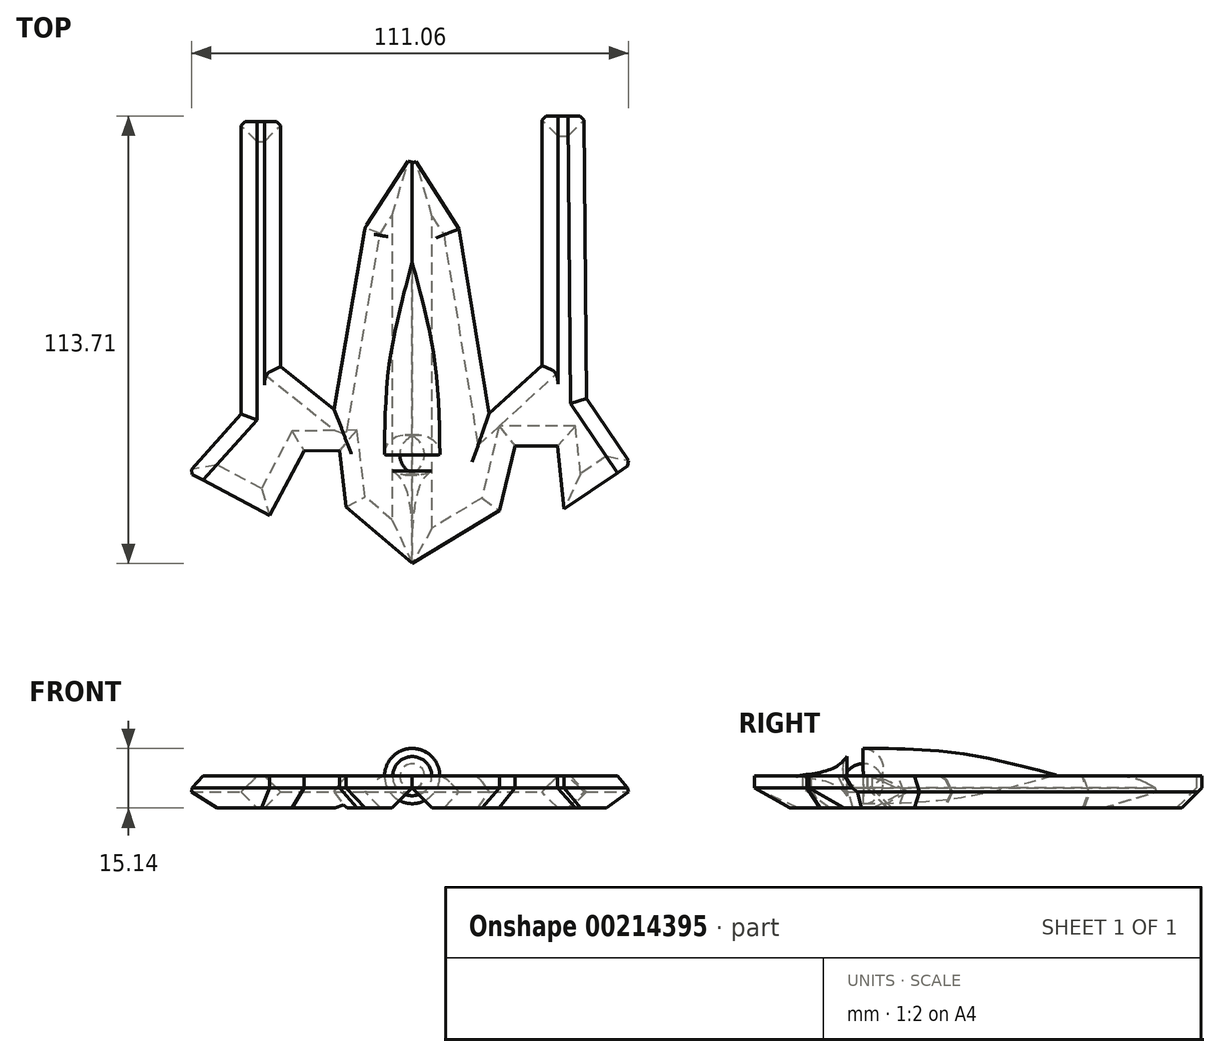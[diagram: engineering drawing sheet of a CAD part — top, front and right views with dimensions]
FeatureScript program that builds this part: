
annotation { "Feature Type Name" : "Feature", "Feature Type Description" : "" }
export const myFeature = defineFeature(function(context is Context, id is Id, definition is map)
    precondition{}
    {
        {
            var Q0;
            Q0=qCreatedBy(makeId("Top.planeOp"),FACE);
            var sketch = newSketch(context, id + "F0", { "sketchPlane" : qUnion([Q0])});
            skLineSegment(sketch, "E0", {"start": v(0, 44.54) * mm, "end": v(12.9, 24.37) * mm});
            skLineSegment(sketch, "E1", {"start": v(12.9, 24.37) * mm, "end": v(20.23, -20.93) * mm});
            skLineSegment(sketch, "E2", {"start": v(20.23, -20.93) * mm, "end": v(20.23, -20.93) * mm});
            skLineSegment(sketch, "E3", {"start": v(20.23, -20.93) * mm, "end": v(31.93, -10.24) * mm});
            skLineSegment(sketch, "E4", {"start": v(31.93, -10.24) * mm, "end": v(31.93, -10.24) * mm});
            skLineSegment(sketch, "E5", {"start": v(31.93, -10.24) * mm, "end": v(31.93, 52.74) * mm});
            skLineSegment(sketch, "E6", {"start": v(31.93, 52.74) * mm, "end": v(44.63, 52.74) * mm});
            skLineSegment(sketch, "E7", {"start": v(44.63, 52.74) * mm, "end": v(45.25, -18.77) * mm});
            skLineSegment(sketch, "E8", {"start": v(45.25, -18.77) * mm, "end": v(56.36, -35.07) * mm});
            skLineSegment(sketch, "E9", {"start": v(56.36, -35.07) * mm, "end": v(38.61, -47.17) * mm});
            skLineSegment(sketch, "E10", {"start": v(38.61, -47.17) * mm, "end": v(36.92, -31.15) * mm});
            skLineSegment(sketch, "E11", {"start": v(36.92, -31.15) * mm, "end": v(26.08, -31.15) * mm});
            skPoint(sketch, "E11.endSnap0", {"position": v(26.08, -15.58) * mm});
            skLineSegment(sketch, "E12", {"start": v(26.08, -31.15) * mm, "end": v(22.14, -47.58) * mm});
            skLineSegment(sketch, "E13", {"start": v(22.14, -47.58) * mm, "end": v(0, -60.97) * mm});
            skLineSegment(sketch, "E14", {"start": v(0, -60.97) * mm, "end": v(0, 44.54) * mm});
            skSolve(sketch);
        }
        {
            var Q0;
            Q0=qCreatedBy(makeId("Top.planeOp"),FACE);
            var sketch = newSketch(context, id + "F1", { "sketchPlane" : qUnion([Q0])});
            skLineSegment(sketch, "E15", {"start": v(0, 44.65) * mm, "end": v(-12.93, 24.7) * mm});
            skLineSegment(sketch, "E16", {"start": v(-12.93, 24.7) * mm, "end": v(-20.5, -19.97) * mm});
            skLineSegment(sketch, "E17", {"start": v(-20.5, -19.97) * mm, "end": v(-32.45, -10.44) * mm});
            skLineSegment(sketch, "E18", {"start": v(-32.45, -10.44) * mm, "end": v(-32.45, 51.3) * mm});
            skLineSegment(sketch, "E19", {"start": v(-32.45, 51.3) * mm, "end": v(-32.45, 51.3) * mm});
            skLineSegment(sketch, "E20", {"start": v(-32.45, 51.3) * mm, "end": v(-44.5, 51.3) * mm});
            skLineSegment(sketch, "E21", {"start": v(-44.5, 51.3) * mm, "end": v(-44.5, 51.3) * mm});
            skLineSegment(sketch, "E22", {"start": v(-44.5, 51.3) * mm, "end": v(-44.5, -22.6) * mm});
            skLineSegment(sketch, "E23", {"start": v(-44.5, -22.6) * mm, "end": v(-57.7, -37.35) * mm});
            skLineSegment(sketch, "E24", {"start": v(-57.7, -37.35) * mm, "end": v(-36.2, -48.81) * mm});
            skLineSegment(sketch, "E25", {"start": v(-36.2, -48.81) * mm, "end": v(-27.46, -32.4) * mm});
            skLineSegment(sketch, "E26", {"start": v(-27.46, -32.4) * mm, "end": v(-18.51, -32.26) * mm});
            skLineSegment(sketch, "E27", {"start": v(-18.51, -32.26) * mm, "end": v(-16.81, -46.65) * mm});
            skLineSegment(sketch, "E28", {"start": v(-16.81, -46.65) * mm, "end": v(0, -60.87) * mm});
            skLineSegment(sketch, "E29", {"start": v(0, -60.87) * mm, "end": v(0, 44.65) * mm});
            skSolve(sketch);
        }
        {
            var Q0;
            Q0 = qSketchRegion(id + "F1", true);
            var Q1;
            Q1=makeQuery(id+"F0.imprint","IMPRINT",FACE,{"disambiguationData":[TD([[makeQuery(id+"F0.imprint","IMPRINT",EDGE,{"derivedFrom":sQuery(id+"F0.wireOp",EDGE,"E0")}),-1.0]])]});
            extrude(context, id + "F9", {"entities" : qUnion([Q0, Q1]), "depth" : 8.14 * mm});
        }
        {
            var Q0;
            Q0=makeQuery(id+"F9.opExtrude","CAP_EDGE",EDGE,{"disambiguationData":[OSD([sQuery(id+"F0.wireOp",EDGE,"E0")])],"isStart":false});
            var Q1;
            Q1=makeQuery(id+"F9.opExtrude","CAP_EDGE",EDGE,{"disambiguationData":[OSD([sQuery(id+"F0.wireOp",EDGE,"E1")])],"isStart":false});
            var Q2;
            Q2=makeQuery(id+"F9.opExtrude","CAP_EDGE",EDGE,{"disambiguationData":[OSD([sQuery(id+"F1.wireOp",EDGE,"E15")])],"isStart":false});
            var Q3;
            Q3=makeQuery(id+"F9.opExtrude","CAP_EDGE",EDGE,{"disambiguationData":[OSD([sQuery(id+"F1.wireOp",EDGE,"E16")])],"isStart":false});
            chamfer(context, id + "F2", {"entities" : qUnion([Q0, Q1, Q2, Q3]), "width" : 5.08 * mm, "tangentPropagation" : true});
        }
        {
            var Q0;
            Q0=makeQuery(id+"F9.opExtrude","CAP_EDGE",EDGE,{"disambiguationData":[OSD([sQuery(id+"F0.wireOp",EDGE,"E5")])],"isStart":false});
            chamfer(context, id + "F3", {"entities" : qUnion([Q0]), "width" : 5.08 * mm, "tangentPropagation" : true});
        }
        {
            var Q0;
            Q0=makeQuery(id+"F9.opExtrude","CAP_EDGE",EDGE,{"disambiguationData":[OSD([sQuery(id+"F0.wireOp",EDGE,"E7")])],"isStart":false});
            chamfer(context, id + "F10", {"entities" : qUnion([Q0]), "width" : 5.08 * mm, "tangentPropagation" : true});
        }
        {
            var Q0;
            Q0=makeQuery(id+"F9.opExtrude","CAP_EDGE",EDGE,{"disambiguationData":[OSD([sQuery(id+"F0.wireOp",EDGE,"E8")])],"isStart":false});
            chamfer(context, id + "F11", {"entities" : qUnion([Q0]), "width" : 5.08 * mm, "tangentPropagation" : true});
        }
        {
            var Q0;
            Q0=makeQuery(id+"F9.opExtrude","CAP_EDGE",EDGE,{"disambiguationData":[OSD([sQuery(id+"F1.wireOp",EDGE,"E23")])],"isStart":false});
            var Q1;
            Q1=makeQuery(id+"F9.opExtrude","CAP_EDGE",EDGE,{"disambiguationData":[OSD([sQuery(id+"F1.wireOp",EDGE,"E22")])],"isStart":false});
            chamfer(context, id + "F4", {"entities" : qUnion([Q0, Q1]), "width" : 5.08 * mm, "tangentPropagation" : true});
        }
        {
            var Q0;
            Q0=makeQuery(id+"F9.opExtrude","CAP_EDGE",EDGE,{"disambiguationData":[OSD([sQuery(id+"F1.wireOp",EDGE,"E18")])],"isStart":false});
            var Q1;
            Q1=makeQuery(id+"F9.opExtrude","CAP_EDGE",EDGE,{"disambiguationData":[OSD([sQuery(id+"F1.wireOp",EDGE,"E17")])],"isStart":false});
            chamfer(context, id + "F5", {"entities" : qUnion([Q0, Q1]), "width" : 5.08 * mm, "tangentPropagation" : true});
        }
        {
            var Q0;
            Q0=makeQuery(id+"F9.opExtrude","CAP_EDGE",EDGE,{"disambiguationData":[OSD([sQuery(id+"F0.wireOp",EDGE,"E3")])],"isStart":false});
            chamfer(context, id + "F6", {"entities" : qUnion([Q0]), "width" : 5.08 * mm, "tangentPropagation" : true});
        }
        {
            var Q0;
            Q0=makeQuery(id+"F9.opExtrude","CAP_FACE",FACE,{"disambiguationData":[OSD([sQuery(id+"F1.wireOp",EDGE,"E15"),sQuery(id+"F1.wireOp",EDGE,"E16"),sQuery(id+"F1.wireOp",EDGE,"E17"),sQuery(id+"F1.wireOp",EDGE,"E18"),sQuery(id+"F1.wireOp",EDGE,"E20"),sQuery(id+"F1.wireOp",EDGE,"E22"),sQuery(id+"F1.wireOp",EDGE,"E23"),sQuery(id+"F1.wireOp",EDGE,"E24"),sQuery(id+"F1.wireOp",EDGE,"E25"),sQuery(id+"F1.wireOp",EDGE,"E26"),sQuery(id+"F1.wireOp",EDGE,"E27"),sQuery(id+"F1.wireOp",EDGE,"E28"),sQuery(id+"F1.wireOp",EDGE,"E29")])],"isStart":true});
            chamfer(context, id + "F12", {"entities" : qUnion([Q0]), "width" : 5.08 * mm, "tangentPropagation" : true});
        }
        {
            var Q0;
            Q0=makeQuery(id+"F9.opExtrude","CAP_FACE",FACE,{"disambiguationData":[OSD([sQuery(id+"F0.wireOp",EDGE,"E0"),sQuery(id+"F0.wireOp",EDGE,"E1"),sQuery(id+"F0.wireOp",EDGE,"E3"),sQuery(id+"F0.wireOp",EDGE,"E5"),sQuery(id+"F0.wireOp",EDGE,"E6"),sQuery(id+"F0.wireOp",EDGE,"E7"),sQuery(id+"F0.wireOp",EDGE,"E8"),sQuery(id+"F0.wireOp",EDGE,"E9"),sQuery(id+"F0.wireOp",EDGE,"E10"),sQuery(id+"F0.wireOp",EDGE,"E11"),sQuery(id+"F0.wireOp",EDGE,"E12"),sQuery(id+"F0.wireOp",EDGE,"E13"),sQuery(id+"F0.wireOp",EDGE,"E14")])],"isStart":true});
            chamfer(context, id + "F13", {"entities" : qUnion([Q0]), "width" : 5.08 * mm, "tangentPropagation" : true});
        }
        {
            var Q0;
            Q0=qCreatedBy(makeId("Right.planeOp"),FACE);
            var sketch = newSketch(context, id + "F14", { "sketchPlane" : qUnion([Q0])});
            skFitSpline(sketch, "E30", {"points": [v(15.67, 8.43) * mm, v(-10.4, 14.09) * mm, v(-36.13, 15.13) * mm], "startDerivative": vector(-51.62, 13.53) * mm, "endDerivative": vector(-51.98, -0.16) * mm});
            skFitSpline(sketch, "E31", {"points": [v(-36.13, 15.13) * mm, v(-40.25, 10.5) * mm, v(-52.55, 8) * mm], "startDerivative": vector(-7.72, -12.68) * mm, "endDerivative": vector(-24.16, -2.19) * mm});
            skLineSegment(sketch, "E32", {"start": v(-52.55, 8) * mm, "end": v(15.67, 8.43) * mm});
            skSolve(sketch);
        }
        {
            var Q0;
            Q0=makeQuery(id+"F14.imprint","IMPRINT",FACE,{"disambiguationData":[TD([[makeQuery(id+"F14.imprint","IMPRINT",EDGE,{"derivedFrom":sQuery(id+"F14.wireOp",EDGE,"E30")}),1.0]])]});
            var Q1;
            Q1=sQuery(id+"F14.wireOp",EDGE,"E32");
            revolve(context, id + "F15", {"entities" : qUnion([Q0]), "axis" : qUnion([Q1]), "revolveType" : RevolveType.FULL});
        }
        {
            var Q0;
            {var subQ0=sQuery(id+"F1.wireOp",EDGE,"E16");Q0=makeQuery(id+"F2.opChamfer","BLEND_EDGE",EDGE,{"blendedFrom":[makeQuery(id+"F9.opExtrude","CAP_EDGE",EDGE,{"disambiguationData":[OSD([subQ0])],"isStart":false}),makeQuery(id+"F9.opExtrude","CAP_FACE",FACE,{"disambiguationData":[OSD([sQuery(id+"F1.wireOp",EDGE,"E15"),subQ0,sQuery(id+"F1.wireOp",EDGE,"E17"),sQuery(id+"F1.wireOp",EDGE,"E18"),sQuery(id+"F1.wireOp",EDGE,"E20"),sQuery(id+"F1.wireOp",EDGE,"E22"),sQuery(id+"F1.wireOp",EDGE,"E23"),sQuery(id+"F1.wireOp",EDGE,"E24"),sQuery(id+"F1.wireOp",EDGE,"E25"),sQuery(id+"F1.wireOp",EDGE,"E26"),sQuery(id+"F1.wireOp",EDGE,"E27"),sQuery(id+"F1.wireOp",EDGE,"E28"),sQuery(id+"F1.wireOp",EDGE,"E29")])],"isStart":false})],"blendedInto":[makeQuery(id+"F9.opExtrude","CAP_FACE",FACE,{"disambiguationData":[OSD([sQuery(id+"F1.wireOp",EDGE,"E15"),subQ0,sQuery(id+"F1.wireOp",EDGE,"E17"),sQuery(id+"F1.wireOp",EDGE,"E18"),sQuery(id+"F1.wireOp",EDGE,"E20"),sQuery(id+"F1.wireOp",EDGE,"E22"),sQuery(id+"F1.wireOp",EDGE,"E23"),sQuery(id+"F1.wireOp",EDGE,"E24"),sQuery(id+"F1.wireOp",EDGE,"E25"),sQuery(id+"F1.wireOp",EDGE,"E26"),sQuery(id+"F1.wireOp",EDGE,"E27"),sQuery(id+"F1.wireOp",EDGE,"E28"),sQuery(id+"F1.wireOp",EDGE,"E29")])],"isStart":false})]});}
            fillet(context, id + "F16", {"entities" : qUnion([Q0]), "radius" : 5.08 * mm, "tangentPropagation" : true, "allowEdgeOverflow" : false});
        }
        {
            var Q0;
            {var subQ0=sQuery(id+"F1.wireOp",EDGE,"E15");Q0=makeQuery(id+"F2.opChamfer","BLEND_EDGE",EDGE,{"blendedFrom":[makeQuery(id+"F9.opExtrude","CAP_EDGE",EDGE,{"disambiguationData":[OSD([subQ0])],"isStart":false}),makeQuery(id+"F9.opExtrude","CAP_FACE",FACE,{"disambiguationData":[OSD([subQ0,sQuery(id+"F1.wireOp",EDGE,"E16"),sQuery(id+"F1.wireOp",EDGE,"E17"),sQuery(id+"F1.wireOp",EDGE,"E18"),sQuery(id+"F1.wireOp",EDGE,"E20"),sQuery(id+"F1.wireOp",EDGE,"E22"),sQuery(id+"F1.wireOp",EDGE,"E23"),sQuery(id+"F1.wireOp",EDGE,"E24"),sQuery(id+"F1.wireOp",EDGE,"E25"),sQuery(id+"F1.wireOp",EDGE,"E26"),sQuery(id+"F1.wireOp",EDGE,"E27"),sQuery(id+"F1.wireOp",EDGE,"E28"),sQuery(id+"F1.wireOp",EDGE,"E29")])],"isStart":false})],"blendedInto":[makeQuery(id+"F9.opExtrude","CAP_FACE",FACE,{"disambiguationData":[OSD([subQ0,sQuery(id+"F1.wireOp",EDGE,"E16"),sQuery(id+"F1.wireOp",EDGE,"E17"),sQuery(id+"F1.wireOp",EDGE,"E18"),sQuery(id+"F1.wireOp",EDGE,"E20"),sQuery(id+"F1.wireOp",EDGE,"E22"),sQuery(id+"F1.wireOp",EDGE,"E23"),sQuery(id+"F1.wireOp",EDGE,"E24"),sQuery(id+"F1.wireOp",EDGE,"E25"),sQuery(id+"F1.wireOp",EDGE,"E26"),sQuery(id+"F1.wireOp",EDGE,"E27"),sQuery(id+"F1.wireOp",EDGE,"E28"),sQuery(id+"F1.wireOp",EDGE,"E29")])],"isStart":false})]});}
            fillet(context, id + "F7", {"entities" : qUnion([Q0]), "radius" : 5.08 * mm, "tangentPropagation" : true, "allowEdgeOverflow" : false});
        }
        {
            var Q0;
            {var subQ0=sQuery(id+"F0.wireOp",EDGE,"E0");Q0=makeQuery(id+"F2.opChamfer","BLEND_EDGE",EDGE,{"blendedFrom":[makeQuery(id+"F9.opExtrude","CAP_EDGE",EDGE,{"disambiguationData":[OSD([subQ0])],"isStart":false}),makeQuery(id+"F9.opExtrude","CAP_FACE",FACE,{"disambiguationData":[OSD([subQ0,sQuery(id+"F0.wireOp",EDGE,"E1"),sQuery(id+"F0.wireOp",EDGE,"E3"),sQuery(id+"F0.wireOp",EDGE,"E5"),sQuery(id+"F0.wireOp",EDGE,"E6"),sQuery(id+"F0.wireOp",EDGE,"E7"),sQuery(id+"F0.wireOp",EDGE,"E8"),sQuery(id+"F0.wireOp",EDGE,"E9"),sQuery(id+"F0.wireOp",EDGE,"E10"),sQuery(id+"F0.wireOp",EDGE,"E11"),sQuery(id+"F0.wireOp",EDGE,"E12"),sQuery(id+"F0.wireOp",EDGE,"E13"),sQuery(id+"F0.wireOp",EDGE,"E14")])],"isStart":false})],"blendedInto":[makeQuery(id+"F9.opExtrude","CAP_FACE",FACE,{"disambiguationData":[OSD([subQ0,sQuery(id+"F0.wireOp",EDGE,"E1"),sQuery(id+"F0.wireOp",EDGE,"E3"),sQuery(id+"F0.wireOp",EDGE,"E5"),sQuery(id+"F0.wireOp",EDGE,"E6"),sQuery(id+"F0.wireOp",EDGE,"E7"),sQuery(id+"F0.wireOp",EDGE,"E8"),sQuery(id+"F0.wireOp",EDGE,"E9"),sQuery(id+"F0.wireOp",EDGE,"E10"),sQuery(id+"F0.wireOp",EDGE,"E11"),sQuery(id+"F0.wireOp",EDGE,"E12"),sQuery(id+"F0.wireOp",EDGE,"E13"),sQuery(id+"F0.wireOp",EDGE,"E14")])],"isStart":false})]});}
            var Q1;
            {var subQ0=sQuery(id+"F0.wireOp",EDGE,"E1");Q1=makeQuery(id+"F2.opChamfer","BLEND_EDGE",EDGE,{"blendedFrom":[makeQuery(id+"F9.opExtrude","CAP_EDGE",EDGE,{"disambiguationData":[OSD([subQ0])],"isStart":false}),makeQuery(id+"F9.opExtrude","CAP_FACE",FACE,{"disambiguationData":[OSD([sQuery(id+"F0.wireOp",EDGE,"E0"),subQ0,sQuery(id+"F0.wireOp",EDGE,"E3"),sQuery(id+"F0.wireOp",EDGE,"E5"),sQuery(id+"F0.wireOp",EDGE,"E6"),sQuery(id+"F0.wireOp",EDGE,"E7"),sQuery(id+"F0.wireOp",EDGE,"E8"),sQuery(id+"F0.wireOp",EDGE,"E9"),sQuery(id+"F0.wireOp",EDGE,"E10"),sQuery(id+"F0.wireOp",EDGE,"E11"),sQuery(id+"F0.wireOp",EDGE,"E12"),sQuery(id+"F0.wireOp",EDGE,"E13"),sQuery(id+"F0.wireOp",EDGE,"E14")])],"isStart":false})],"blendedInto":[makeQuery(id+"F9.opExtrude","CAP_FACE",FACE,{"disambiguationData":[OSD([sQuery(id+"F0.wireOp",EDGE,"E0"),subQ0,sQuery(id+"F0.wireOp",EDGE,"E3"),sQuery(id+"F0.wireOp",EDGE,"E5"),sQuery(id+"F0.wireOp",EDGE,"E6"),sQuery(id+"F0.wireOp",EDGE,"E7"),sQuery(id+"F0.wireOp",EDGE,"E8"),sQuery(id+"F0.wireOp",EDGE,"E9"),sQuery(id+"F0.wireOp",EDGE,"E10"),sQuery(id+"F0.wireOp",EDGE,"E11"),sQuery(id+"F0.wireOp",EDGE,"E12"),sQuery(id+"F0.wireOp",EDGE,"E13"),sQuery(id+"F0.wireOp",EDGE,"E14")])],"isStart":false})]});}
            fillet(context, id + "F8", {"entities" : qUnion([Q0, Q1]), "radius" : 5.08 * mm, "tangentPropagation" : true, "allowEdgeOverflow" : false});
        }
        {
            var Q0;
            {var subQ0=sQuery(id+"F1.wireOp",EDGE,"E17");Q0=makeQuery(id+"F5.opChamfer","BLEND_EDGE",EDGE,{"blendedFrom":[makeQuery(id+"F9.opExtrude","CAP_EDGE",EDGE,{"disambiguationData":[OSD([subQ0])],"isStart":false}),makeQuery(id+"F9.opExtrude","CAP_FACE",FACE,{"disambiguationData":[OSD([sQuery(id+"F1.wireOp",EDGE,"E15"),sQuery(id+"F1.wireOp",EDGE,"E16"),subQ0,sQuery(id+"F1.wireOp",EDGE,"E18"),sQuery(id+"F1.wireOp",EDGE,"E20"),sQuery(id+"F1.wireOp",EDGE,"E22"),sQuery(id+"F1.wireOp",EDGE,"E23"),sQuery(id+"F1.wireOp",EDGE,"E24"),sQuery(id+"F1.wireOp",EDGE,"E25"),sQuery(id+"F1.wireOp",EDGE,"E26"),sQuery(id+"F1.wireOp",EDGE,"E27"),sQuery(id+"F1.wireOp",EDGE,"E28"),sQuery(id+"F1.wireOp",EDGE,"E29")])],"isStart":false})],"blendedInto":[makeQuery(id+"F9.opExtrude","CAP_FACE",FACE,{"disambiguationData":[OSD([sQuery(id+"F1.wireOp",EDGE,"E15"),sQuery(id+"F1.wireOp",EDGE,"E16"),subQ0,sQuery(id+"F1.wireOp",EDGE,"E18"),sQuery(id+"F1.wireOp",EDGE,"E20"),sQuery(id+"F1.wireOp",EDGE,"E22"),sQuery(id+"F1.wireOp",EDGE,"E23"),sQuery(id+"F1.wireOp",EDGE,"E24"),sQuery(id+"F1.wireOp",EDGE,"E25"),sQuery(id+"F1.wireOp",EDGE,"E26"),sQuery(id+"F1.wireOp",EDGE,"E27"),sQuery(id+"F1.wireOp",EDGE,"E28"),sQuery(id+"F1.wireOp",EDGE,"E29")])],"isStart":false})]});}
            fillet(context, id + "F17", {"entities" : qUnion([Q0]), "radius" : 5.08 * mm, "tangentPropagation" : true, "allowEdgeOverflow" : false});
        }
        {
            var Q0;
            {var subQ0=sQuery(id+"F0.wireOp",EDGE,"E3");Q0=makeQuery(id+"F6.opChamfer","BLEND_EDGE",EDGE,{"blendedFrom":[makeQuery(id+"F9.opExtrude","CAP_EDGE",EDGE,{"disambiguationData":[OSD([subQ0])],"isStart":false}),makeQuery(id+"F9.opExtrude","CAP_FACE",FACE,{"disambiguationData":[OSD([sQuery(id+"F0.wireOp",EDGE,"E0"),sQuery(id+"F0.wireOp",EDGE,"E1"),subQ0,sQuery(id+"F0.wireOp",EDGE,"E5"),sQuery(id+"F0.wireOp",EDGE,"E6"),sQuery(id+"F0.wireOp",EDGE,"E7"),sQuery(id+"F0.wireOp",EDGE,"E8"),sQuery(id+"F0.wireOp",EDGE,"E9"),sQuery(id+"F0.wireOp",EDGE,"E10"),sQuery(id+"F0.wireOp",EDGE,"E11"),sQuery(id+"F0.wireOp",EDGE,"E12"),sQuery(id+"F0.wireOp",EDGE,"E13"),sQuery(id+"F0.wireOp",EDGE,"E14")])],"isStart":false})],"blendedInto":[makeQuery(id+"F9.opExtrude","CAP_FACE",FACE,{"disambiguationData":[OSD([sQuery(id+"F0.wireOp",EDGE,"E0"),sQuery(id+"F0.wireOp",EDGE,"E1"),subQ0,sQuery(id+"F0.wireOp",EDGE,"E5"),sQuery(id+"F0.wireOp",EDGE,"E6"),sQuery(id+"F0.wireOp",EDGE,"E7"),sQuery(id+"F0.wireOp",EDGE,"E8"),sQuery(id+"F0.wireOp",EDGE,"E9"),sQuery(id+"F0.wireOp",EDGE,"E10"),sQuery(id+"F0.wireOp",EDGE,"E11"),sQuery(id+"F0.wireOp",EDGE,"E12"),sQuery(id+"F0.wireOp",EDGE,"E13"),sQuery(id+"F0.wireOp",EDGE,"E14")])],"isStart":false})]});}
            fillet(context, id + "F18", {"entities" : qUnion([Q0]), "radius" : 5.08 * mm, "tangentPropagation" : true, "allowEdgeOverflow" : false});
        }
        {
            var Q0;
            Q0=makeQuery(id+"F15.opRevolve","SWEPT_EDGE",EDGE,{"disambiguationData":[OSD([sQuery(id+"F14.wireOp",EDGE,"E30"),sQuery(id+"F14.wireOp",EDGE,"E31")])]});
            fillet(context, id + "F19", {"entities" : qUnion([Q0]), "radius" : 5.08 * mm, "tangentPropagation" : true, "allowEdgeOverflow" : false});
        }
    });
